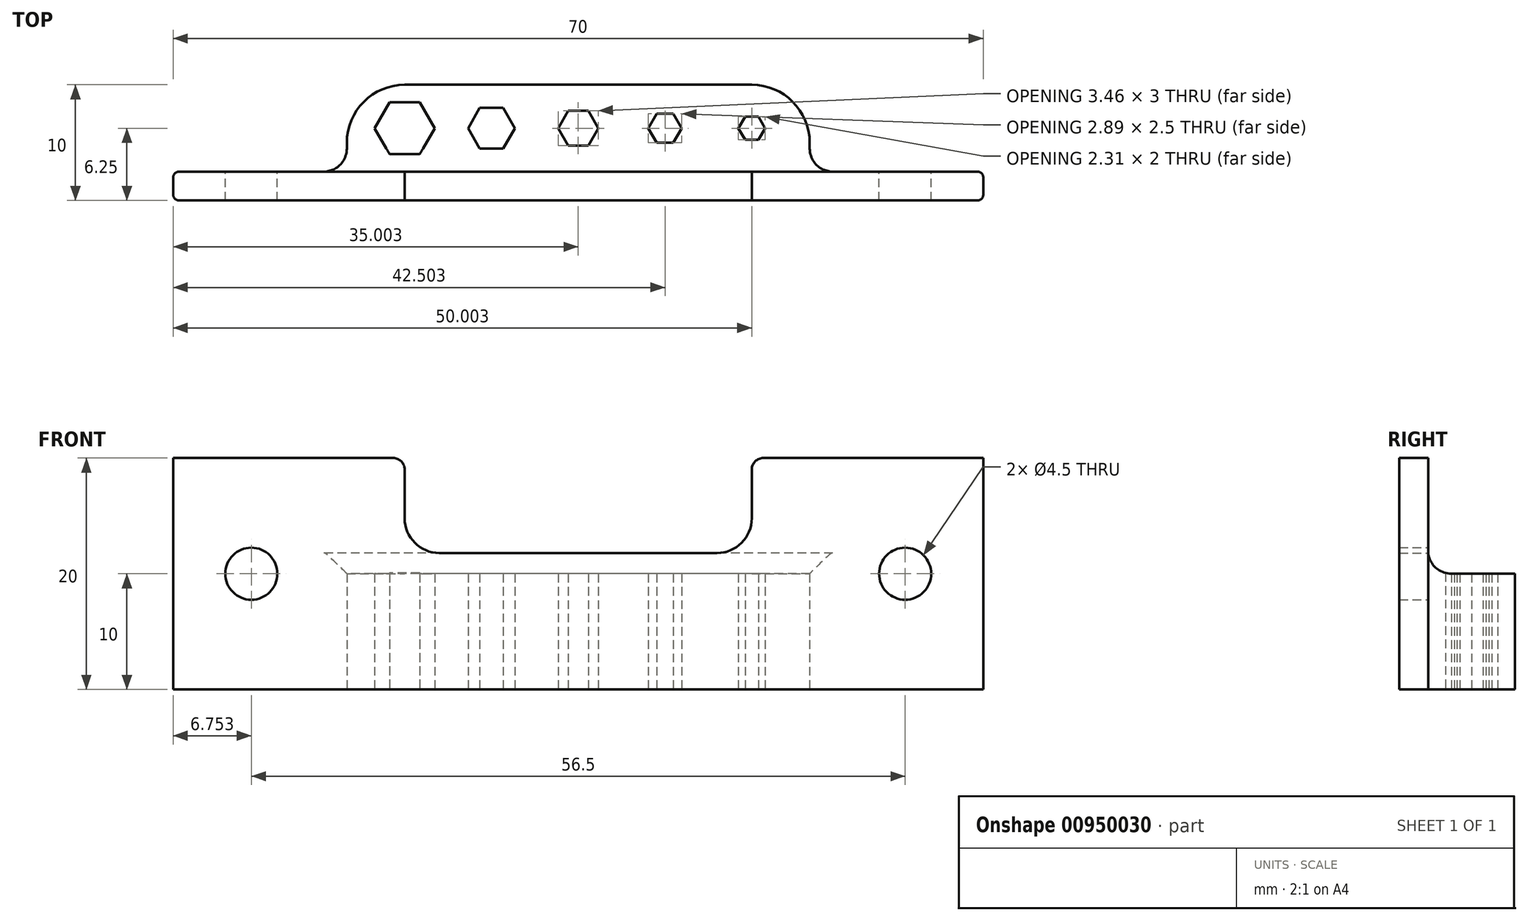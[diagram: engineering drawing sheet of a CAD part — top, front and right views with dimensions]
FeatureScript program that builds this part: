
annotation { "Feature Type Name" : "Feature", "Feature Type Description" : "" }
export const myFeature = defineFeature(function(context is Context, id is Id, definition is map)
    precondition{}
    {
        {
            var Q0;
            Q0=qCreatedBy(makeId("Top.planeOp"),FACE);
            var sketch = newSketch(context, id + "F0", { "sketchPlane" : qUnion([Q0])});
            skLineSegment(sketch, "E0", {"start": v(-14.17, 0.5) * mm, "end": v(-14.17, 2) * mm});
            skLineSegment(sketch, "E1", {"start": v(-13.67, 2.5) * mm, "end": v(-1.17, 2.5) * mm});
            skLineSegment(sketch, "E2", {"start": v(0.83, 4.5) * mm, "end": v(0.83, 5) * mm});
            skLineSegment(sketch, "E3", {"start": v(5.83, 10) * mm, "end": v(35.83, 10) * mm});
            skLineSegment(sketch, "E4", {"start": v(40.83, 5) * mm, "end": v(40.83, 4.5) * mm});
            skLineSegment(sketch, "E5", {"start": v(42.83, 2.5) * mm, "end": v(55.33, 2.5) * mm});
            skLineSegment(sketch, "E6", {"start": v(55.83, 2) * mm, "end": v(55.83, 0.5) * mm});
            skLineSegment(sketch, "E7", {"start": v(55.33, 0) * mm, "end": v(-13.67, 0) * mm});
            skLineSegment(sketch, "E8", {"start": v(0.83, 6.25) * mm, "end": v(40.83, 6.25) * mm, "construction": true});
            skLineSegment(sketch, "E9", {"start": v(5.83, 6.25) * mm, "end": v(5.83, 10) * mm, "construction": true});
            skLineSegment(sketch, "E10", {"start": v(13.33, 6.25) * mm, "end": v(13.33, 10) * mm, "construction": true});
            skLineSegment(sketch, "E11", {"start": v(20.83, 6.25) * mm, "end": v(20.83, 10) * mm, "construction": true});
            skLineSegment(sketch, "E12", {"start": v(28.33, 6.25) * mm, "end": v(28.33, 10) * mm, "construction": true});
            skLineSegment(sketch, "E13", {"start": v(35.83, 6.25) * mm, "end": v(35.83, 10) * mm, "construction": true});
            skLineSegment(sketch, "E14.0", {"start": v(4.68, 8.25) * mm, "end": v(6.99, 8.25) * mm, "construction": true});
            skLineSegment(sketch, "E14.1", {"start": v(6.99, 8.25) * mm, "end": v(8.14, 6.25) * mm, "construction": true});
            skLineSegment(sketch, "E14.2", {"start": v(8.14, 6.25) * mm, "end": v(6.99, 4.25) * mm, "construction": true});
            skLineSegment(sketch, "E14.3", {"start": v(6.99, 4.25) * mm, "end": v(4.68, 4.25) * mm, "construction": true});
            skLineSegment(sketch, "E14.4", {"start": v(4.68, 4.25) * mm, "end": v(3.52, 6.25) * mm, "construction": true});
            skLineSegment(sketch, "E14.5", {"start": v(3.52, 6.25) * mm, "end": v(4.68, 8.25) * mm, "construction": true});
            skPoint(sketch, "E14.0.midPoint", {"position": v(5.83, 8.25) * mm});
            skLineSegment(sketch, "E15.0", {"start": v(12.47, 7.75) * mm, "end": v(14.2, 7.75) * mm, "construction": true});
            skLineSegment(sketch, "E15.1", {"start": v(14.2, 7.75) * mm, "end": v(15.07, 6.25) * mm, "construction": true});
            skLineSegment(sketch, "E15.2", {"start": v(15.07, 6.25) * mm, "end": v(14.2, 4.75) * mm, "construction": true});
            skLineSegment(sketch, "E15.3", {"start": v(14.2, 4.75) * mm, "end": v(12.47, 4.75) * mm, "construction": true});
            skLineSegment(sketch, "E15.4", {"start": v(12.47, 4.75) * mm, "end": v(11.6, 6.25) * mm, "construction": true});
            skLineSegment(sketch, "E15.5", {"start": v(11.6, 6.25) * mm, "end": v(12.47, 7.75) * mm, "construction": true});
            skPoint(sketch, "E15.0.midPoint", {"position": v(13.33, 7.75) * mm});
            skLineSegment(sketch, "E16.0", {"start": v(20.11, 7.5) * mm, "end": v(21.56, 7.5) * mm, "construction": true});
            skLineSegment(sketch, "E16.1", {"start": v(21.56, 7.5) * mm, "end": v(22.28, 6.25) * mm, "construction": true});
            skLineSegment(sketch, "E16.2", {"start": v(22.28, 6.25) * mm, "end": v(21.56, 5) * mm, "construction": true});
            skLineSegment(sketch, "E16.3", {"start": v(21.56, 5) * mm, "end": v(20.11, 5) * mm, "construction": true});
            skLineSegment(sketch, "E16.4", {"start": v(20.11, 5) * mm, "end": v(19.39, 6.25) * mm, "construction": true});
            skLineSegment(sketch, "E16.5", {"start": v(19.39, 6.25) * mm, "end": v(20.11, 7.5) * mm, "construction": true});
            skPoint(sketch, "E16.0.midPoint", {"position": v(20.83, 7.5) * mm});
            skLineSegment(sketch, "E17.0", {"start": v(27.76, 7.25) * mm, "end": v(28.91, 7.25) * mm, "construction": true});
            skLineSegment(sketch, "E17.1", {"start": v(28.91, 7.25) * mm, "end": v(29.49, 6.25) * mm, "construction": true});
            skLineSegment(sketch, "E17.2", {"start": v(29.49, 6.25) * mm, "end": v(28.91, 5.25) * mm, "construction": true});
            skLineSegment(sketch, "E17.3", {"start": v(28.91, 5.25) * mm, "end": v(27.76, 5.25) * mm, "construction": true});
            skLineSegment(sketch, "E17.4", {"start": v(27.76, 5.25) * mm, "end": v(27.18, 6.25) * mm, "construction": true});
            skLineSegment(sketch, "E17.5", {"start": v(27.18, 6.25) * mm, "end": v(27.76, 7.25) * mm, "construction": true});
            skPoint(sketch, "E17.0.midPoint", {"position": v(28.33, 7.25) * mm});
            skLineSegment(sketch, "E18.0", {"start": v(35.4, 7) * mm, "end": v(36.27, 7) * mm, "construction": true});
            skLineSegment(sketch, "E18.1", {"start": v(36.27, 7) * mm, "end": v(36.7, 6.25) * mm, "construction": true});
            skLineSegment(sketch, "E18.2", {"start": v(36.7, 6.25) * mm, "end": v(36.27, 5.5) * mm, "construction": true});
            skLineSegment(sketch, "E18.3", {"start": v(36.27, 5.5) * mm, "end": v(35.4, 5.5) * mm, "construction": true});
            skLineSegment(sketch, "E18.4", {"start": v(35.4, 5.5) * mm, "end": v(34.97, 6.25) * mm, "construction": true});
            skLineSegment(sketch, "E18.5", {"start": v(34.97, 6.25) * mm, "end": v(35.4, 7) * mm, "construction": true});
            skPoint(sketch, "E18.0.midPoint", {"position": v(35.83, 7) * mm});
            skPoint(sketch, "E19.visualSharp", {"position": v(0.83, 2.5) * mm});
            skArc(sketch, "E19.filletArc", {"start": v(-1.17, 2.5) * mm, "mid": v(0.25, 3.09) * mm, "end": v(0.83, 4.5) * mm});
            skPoint(sketch, "E20.visualSharp", {"position": v(40.83, 2.5) * mm});
            skArc(sketch, "E20.filletArc", {"start": v(40.83, 4.5) * mm, "mid": v(41.42, 3.09) * mm, "end": v(42.83, 2.5) * mm});
            skPoint(sketch, "E21.visualSharp", {"position": v(-14.17, 2.5) * mm});
            skArc(sketch, "E21.filletArc", {"start": v(-13.67, 2.5) * mm, "mid": v(-14.02, 2.35) * mm, "end": v(-14.17, 2) * mm});
            skPoint(sketch, "E22.visualSharp", {"position": v(-14.17, 0) * mm});
            skArc(sketch, "E22.filletArc", {"start": v(-14.17, 0.5) * mm, "mid": v(-14.02, 0.15) * mm, "end": v(-13.67, 0) * mm});
            skPoint(sketch, "E23.visualSharp", {"position": v(55.83, 0) * mm});
            skArc(sketch, "E23.filletArc", {"start": v(55.33, 0) * mm, "mid": v(55.69, 0.15) * mm, "end": v(55.83, 0.5) * mm});
            skPoint(sketch, "E24.visualSharp", {"position": v(55.83, 2.5) * mm});
            skArc(sketch, "E24.filletArc", {"start": v(55.83, 2) * mm, "mid": v(55.69, 2.35) * mm, "end": v(55.33, 2.5) * mm});
            skPoint(sketch, "E25.visualSharp", {"position": v(0.83, 10) * mm});
            skArc(sketch, "E25.filletArc", {"start": v(5.83, 10) * mm, "mid": v(2.3, 8.54) * mm, "end": v(0.83, 5) * mm});
            skPoint(sketch, "E26.visualSharp", {"position": v(40.83, 10) * mm});
            skArc(sketch, "E26.filletArc", {"start": v(40.83, 5) * mm, "mid": v(39.37, 8.54) * mm, "end": v(35.83, 10) * mm});
            skCircle(sketch, "E27", {"center": v(5.83, 6.25) * mm, "radius": 2.25 * mm, "construction": true});
            skCircle(sketch, "E28", {"center": v(13.33, 6.25) * mm, "radius": 1.75 * mm, "construction": true});
            skCircle(sketch, "E29", {"center": v(20.83, 6.25) * mm, "radius": 1.5 * mm, "construction": true});
            skCircle(sketch, "E30", {"center": v(28.33, 6.25) * mm, "radius": 1.25 * mm, "construction": true});
            skCircle(sketch, "E31", {"center": v(35.83, 6.25) * mm, "radius": 1 * mm, "construction": true});
            skLineSegment(sketch, "E32.0", {"start": v(4.53, 8.5) * mm, "end": v(7.13, 8.5) * mm});
            skLineSegment(sketch, "E32.1", {"start": v(7.13, 8.5) * mm, "end": v(8.43, 6.25) * mm});
            skLineSegment(sketch, "E32.2", {"start": v(8.43, 6.25) * mm, "end": v(7.13, 4) * mm});
            skLineSegment(sketch, "E32.3", {"start": v(7.13, 4) * mm, "end": v(4.53, 4) * mm});
            skLineSegment(sketch, "E32.4", {"start": v(4.53, 4) * mm, "end": v(3.24, 6.25) * mm});
            skLineSegment(sketch, "E32.5", {"start": v(3.24, 6.25) * mm, "end": v(4.53, 8.5) * mm});
            skPoint(sketch, "E32.0.midPoint", {"position": v(5.83, 8.5) * mm});
            skLineSegment(sketch, "E33.0", {"start": v(12.32, 8) * mm, "end": v(14.34, 8) * mm});
            skLineSegment(sketch, "E33.1", {"start": v(14.34, 8) * mm, "end": v(15.35, 6.25) * mm});
            skLineSegment(sketch, "E33.2", {"start": v(15.35, 6.25) * mm, "end": v(14.34, 4.5) * mm});
            skLineSegment(sketch, "E33.3", {"start": v(14.34, 4.5) * mm, "end": v(12.32, 4.5) * mm});
            skLineSegment(sketch, "E33.4", {"start": v(12.32, 4.5) * mm, "end": v(11.31, 6.25) * mm});
            skLineSegment(sketch, "E33.5", {"start": v(11.31, 6.25) * mm, "end": v(12.32, 8) * mm});
            skPoint(sketch, "E33.0.midPoint", {"position": v(13.33, 8) * mm});
            skLineSegment(sketch, "E34.0", {"start": v(19.97, 7.75) * mm, "end": v(21.7, 7.75) * mm});
            skLineSegment(sketch, "E34.1", {"start": v(21.7, 7.75) * mm, "end": v(22.57, 6.25) * mm});
            skLineSegment(sketch, "E34.2", {"start": v(22.57, 6.25) * mm, "end": v(21.7, 4.75) * mm});
            skLineSegment(sketch, "E34.3", {"start": v(21.7, 4.75) * mm, "end": v(19.97, 4.75) * mm});
            skLineSegment(sketch, "E34.4", {"start": v(19.97, 4.75) * mm, "end": v(19.1, 6.25) * mm});
            skLineSegment(sketch, "E34.5", {"start": v(19.1, 6.25) * mm, "end": v(19.97, 7.75) * mm});
            skPoint(sketch, "E34.0.midPoint", {"position": v(20.83, 7.75) * mm});
            skLineSegment(sketch, "E35.0", {"start": v(27.61, 7.5) * mm, "end": v(29.06, 7.5) * mm});
            skLineSegment(sketch, "E35.1", {"start": v(29.06, 7.5) * mm, "end": v(29.78, 6.25) * mm});
            skLineSegment(sketch, "E35.2", {"start": v(29.78, 6.25) * mm, "end": v(29.06, 5) * mm});
            skLineSegment(sketch, "E35.3", {"start": v(29.06, 5) * mm, "end": v(27.61, 5) * mm});
            skLineSegment(sketch, "E35.4", {"start": v(27.61, 5) * mm, "end": v(26.89, 6.25) * mm});
            skLineSegment(sketch, "E35.5", {"start": v(26.89, 6.25) * mm, "end": v(27.61, 7.5) * mm});
            skPoint(sketch, "E35.0.midPoint", {"position": v(28.33, 7.5) * mm});
            skLineSegment(sketch, "E36.0", {"start": v(35.26, 7.25) * mm, "end": v(36.41, 7.25) * mm});
            skLineSegment(sketch, "E36.1", {"start": v(36.41, 7.25) * mm, "end": v(36.99, 6.25) * mm});
            skLineSegment(sketch, "E36.2", {"start": v(36.99, 6.25) * mm, "end": v(36.41, 5.25) * mm});
            skLineSegment(sketch, "E36.3", {"start": v(36.41, 5.25) * mm, "end": v(35.26, 5.25) * mm});
            skLineSegment(sketch, "E36.4", {"start": v(35.26, 5.25) * mm, "end": v(34.68, 6.25) * mm});
            skLineSegment(sketch, "E36.5", {"start": v(34.68, 6.25) * mm, "end": v(35.26, 7.25) * mm});
            skPoint(sketch, "E36.0.midPoint", {"position": v(35.83, 7.25) * mm});
            skSolve(sketch);
        }
        {
            var Q0;
            Q0=makeQuery(id+"F0.imprint","IMPRINT",FACE,{"disambiguationData":[TD([[makeQuery(id+"F0.imprint","IMPRINT",EDGE,{"derivedFrom":sQuery(id+"F0.wireOp",EDGE,"E0")}),-1.0]])]});
            extrude(context, id + "F1", {"entities" : qUnion([Q0]), "depth" : 20 * mm, "offsetDistance" : 25 * mm});
        }
        {
            var Q0;
            Q0=makeQuery(id+"F1.opExtrude","SWEPT_FACE",FACE,{"disambiguationData":[OSD([sQuery(id+"F0.wireOp",EDGE,"E1")])]});
            var sketch = newSketch(context, id + "F2", { "sketchPlane" : qUnion([Q0])});
            skPoint(sketch, "E37.0", {"position": v(-55.33, 10) * mm});
            skPoint(sketch, "E38.0", {"position": v(-42.83, 10) * mm});
            skLineSegment(sketch, "E39", {"start": v(-42.83, 10) * mm, "end": v(-55.33, 10) * mm, "construction": true});
            skPoint(sketch, "E40.0", {"position": v(13.67, 10) * mm});
            skPoint(sketch, "E41.0", {"position": v(1.17, 10) * mm});
            skLineSegment(sketch, "E42", {"start": v(13.67, 10) * mm, "end": v(1.17, 10) * mm, "construction": true});
            skCircle(sketch, "E43", {"center": v(7.42, 10) * mm, "radius": 2.25 * mm});
            skCircle(sketch, "E44", {"center": v(-49.08, 10) * mm, "radius": 2.25 * mm});
            skSolve(sketch);
        }
        {
            var Q0;
            Q0=makeQuery(id+"F2.imprint","IMPRINT",FACE,{"disambiguationData":[TD([[makeQuery(id+"F2.imprint","IMPRINT",EDGE,{"derivedFrom":sQuery(id+"F2.wireOp",EDGE,"E43")}),1.0]])]});
            var Q1;
            Q1=makeQuery(id+"F2.imprint","IMPRINT",FACE,{"disambiguationData":[TD([[makeQuery(id+"F2.imprint","IMPRINT",EDGE,{"derivedFrom":sQuery(id+"F2.wireOp",EDGE,"E44")}),1.0]])]});
            extrude(context, id + "F3", {"entities" : qUnion([Q0, Q1]), "operationType" : NewBodyOperationType.REMOVE, "oppositeDirection" : true, "depth" : 25 * mm, "offsetDistance" : 25 * mm});
        }
        {
            var Q0;
            Q0=makeQuery(id+"F1.opExtrude","SWEPT_FACE",FACE,{"disambiguationData":[OSD([sQuery(id+"F0.wireOp",EDGE,"E2")])]});
            var sketch = newSketch(context, id + "F4", { "sketchPlane" : qUnion([Q0])});
            skLineSegment(sketch, "E45.0", {"start": v(-2.5, 20) * mm, "end": v(-2.5, 11.8) * mm});
            skLineSegment(sketch, "E46.0", {"start": v(-10, 20) * mm, "end": v(-10, 0) * mm});
            skLineSegment(sketch, "E47", {"start": v(-10, 10) * mm, "end": v(-4.5, 10) * mm});
            skArc(sketch, "E48", {"start": v(-4.5, 10) * mm, "mid": v(-3, 10.67) * mm, "end": v(-2.5, 12.23) * mm});
            skPoint(sketch, "E49.orphan", {"position": v(-2.5, 0) * mm});
            skLineSegment(sketch, "E50", {"start": v(-10, 20) * mm, "end": v(-2.5, 20) * mm});
            skSolve(sketch);
        }
        {
            var Q0;
            Q0=makeQuery(id+"F1.opExtrude","SWEPT_FACE",FACE,{"disambiguationData":[OSD([sQuery(id+"F0.wireOp",EDGE,"E0")])]});
            var sketch = newSketch(context, id + "F5", { "sketchPlane" : qUnion([Q0])});
            skLineSegment(sketch, "E51.0", {"start": v(-2.5, 20) * mm, "end": v(-2.5, 11.8) * mm});
            skArc(sketch, "E51.1", {"start": v(-4.5, 10) * mm, "mid": v(-3, 10.67) * mm, "end": v(-2.5, 12.23) * mm});
            skLineSegment(sketch, "E51.2", {"start": v(-10, 10) * mm, "end": v(-4.5, 10) * mm});
            skLineSegment(sketch, "E51.3", {"start": v(-10, 20) * mm, "end": v(-10, 0) * mm});
            skLineSegment(sketch, "E51.4", {"start": v(-10, 20) * mm, "end": v(-2.5, 20) * mm});
            skSolve(sketch);
        }
        {
            var Q0;
            {var subQ0=sQuery(id+"F5.wireOp",EDGE,"E51.2");Q0=makeQuery(id+"F5.imprint","IMPRINT",FACE,{"disambiguationData":[TD([[makeQuery(id+"F5.imprint","IMPRINT",EDGE,{"derivedFrom":subQ0}),1.0]])]});}
            extrude(context, id + "F6", {"entities" : qUnion([Q0]), "operationType" : NewBodyOperationType.REMOVE, "oppositeDirection" : true, "depth" : 200 * mm, "offsetDistance" : 25 * mm});
        }
        {
            var Q0;
            Q0=makeQuery(id+"F6.boolean.opBoolean","MERGE",FACE,{"derivedFrom":[makeQuery(id+"F1.opExtrude","SWEPT_FACE",FACE,{"disambiguationData":[OSD([sQuery(id+"F0.wireOp",EDGE,"E1")])]}),makeQuery(id+"F1.opExtrude","SWEPT_FACE",FACE,{"disambiguationData":[OSD([sQuery(id+"F0.wireOp",EDGE,"E5")])]})],"fromTools":[makeQuery(id+"F6.opExtrude","SWEPT_FACE",FACE,{"disambiguationData":[OSD([sQuery(id+"F5.wireOp",EDGE,"E51.0")])]})]});
            var sketch = newSketch(context, id + "F7", { "sketchPlane" : qUnion([Q0])});
            skLineSegment(sketch, "E52.0", {"start": v(-35.83, 10) * mm, "end": v(-35.83, 0) * mm});
            skLineSegment(sketch, "E52.1", {"start": v(-5.83, 10) * mm, "end": v(-5.83, 0) * mm});
            skLineSegment(sketch, "E53.bottom", {"start": v(-35.83, 20) * mm, "end": v(-5.83, 20) * mm});
            skLineSegment(sketch, "E53.top", {"start": v(-32.83, 11.8) * mm, "end": v(-8.83, 11.8) * mm});
            skLineSegment(sketch, "E53.left", {"start": v(-35.83, 19) * mm, "end": v(-35.83, 14.8) * mm});
            skLineSegment(sketch, "E53.right", {"start": v(-5.83, 19) * mm, "end": v(-5.83, 14.8) * mm});
            skPoint(sketch, "E54.visualSharp", {"position": v(-35.83, 11.8) * mm});
            skArc(sketch, "E54.filletArc", {"start": v(-35.83, 14.8) * mm, "mid": v(-34.95, 12.67) * mm, "end": v(-32.83, 11.8) * mm});
            skPoint(sketch, "E55.visualSharp", {"position": v(-5.83, 11.8) * mm});
            skArc(sketch, "E55.filletArc", {"start": v(-8.83, 11.8) * mm, "mid": v(-6.71, 12.67) * mm, "end": v(-5.83, 14.8) * mm});
            skLineSegment(sketch, "E56.0", {"start": v(13.67, 20) * mm, "end": v(-4.83, 20) * mm});
            skLineSegment(sketch, "E57", {"start": v(-36.83, 20) * mm, "end": v(-55.33, 20) * mm});
            skLineSegment(sketch, "E58", {"start": v(-5.83, 20) * mm, "end": v(-35.83, 20) * mm});
            skPoint(sketch, "E59.visualSharp", {"position": v(-35.83, 20) * mm});
            skArc(sketch, "E59.filletArc", {"start": v(-35.83, 19) * mm, "mid": v(-36.13, 19.7) * mm, "end": v(-36.83, 20) * mm});
            skPoint(sketch, "E60.visualSharp", {"position": v(-5.83, 20) * mm});
            skArc(sketch, "E60.filletArc", {"start": v(-4.83, 20) * mm, "mid": v(-5.54, 19.7) * mm, "end": v(-5.83, 19) * mm});
            skSolve(sketch);
        }
        {
            var Q0;
            Q0=makeQuery(id+"F7.imprint","IMPRINT",FACE,{"disambiguationData":[TD([[makeQuery(id+"F7.imprint","IMPRINT",EDGE,{"derivedFrom":sQuery(id+"F7.wireOp",EDGE,"E53.top")}),1.0]])]});
            extrude(context, id + "F8", {"entities" : qUnion([Q0]), "operationType" : NewBodyOperationType.REMOVE, "oppositeDirection" : true, "depth" : 25 * mm, "offsetDistance" : 25 * mm});
        }
    });
